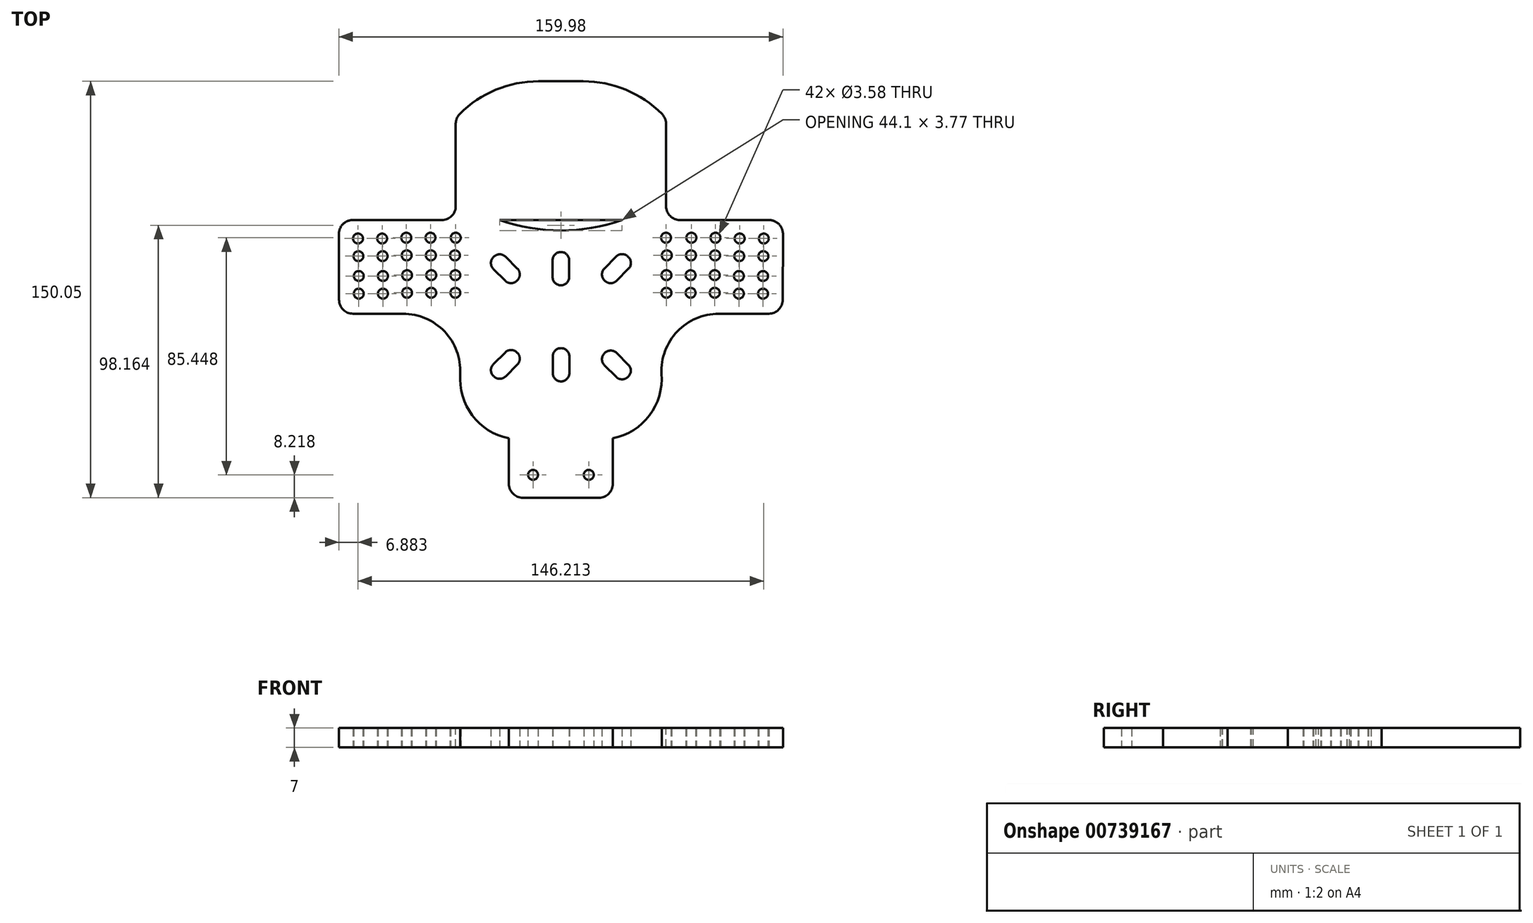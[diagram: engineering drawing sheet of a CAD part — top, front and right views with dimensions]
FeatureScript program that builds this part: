
annotation { "Feature Type Name" : "Feature", "Feature Type Description" : "" }
export const myFeature = defineFeature(function(context is Context, id is Id, definition is map)
    precondition{}
    {
        {
            var Q0;
            Q0=qCreatedBy(makeId("Top.planeOp"),FACE);
            var sketch = newSketch(context, id + "F0", { "sketchPlane" : qUnion([Q0])});
            skLineSegment(sketch, "E0", {"start": v(-79.91, 0) * mm, "end": v(79.75, 0) * mm, "construction": true});
            skLineSegment(sketch, "E1", {"start": v(-22.05, 33.69) * mm, "end": v(-80, 33.69) * mm});
            skLineSegment(sketch, "E2", {"start": v(-80, 33.69) * mm, "end": v(-79.91, -0.06) * mm});
            skLineSegment(sketch, "E3", {"start": v(-79.91, -0.06) * mm, "end": v(-56.88, -0.06) * mm});
            skArc(sketch, "E4", {"start": v(-36.27, -21.72) * mm, "mid": v(-41.93, -6.47) * mm, "end": v(-56.88, -0.06) * mm});
            skArc(sketch, "E5", {"start": v(-36.27, -21.72) * mm, "mid": v(-31.92, -36.69) * mm, "end": v(-18.73, -45) * mm});
            skLineSegment(sketch, "E6", {"start": v(-18.73, -45) * mm, "end": v(-18.73, -66.36) * mm});
            skLineSegment(sketch, "E7", {"start": v(-18.73, -66.36) * mm, "end": v(0, -66.36) * mm});
            skCircle(sketch, "E8", {"center": v(-73.1, 27.02) * mm, "radius": 1.8 * mm});
            skCircle(sketch, "E9", {"center": v(-72.82, 13.52) * mm, "radius": 1.8 * mm});
            skCircle(sketch, "E10", {"center": v(-72.95, 20.67) * mm, "radius": 1.8 * mm});
            skCircle(sketch, "E11", {"center": v(-72.82, 7.17) * mm, "radius": 1.8 * mm});
            skCircle(sketch, "E12", {"center": v(-64.4, 27.02) * mm, "radius": 1.8 * mm});
            skCircle(sketch, "E13", {"center": v(-64.12, 13.52) * mm, "radius": 1.8 * mm});
            skCircle(sketch, "E14", {"center": v(-64.25, 20.67) * mm, "radius": 1.8 * mm});
            skCircle(sketch, "E15", {"center": v(-64.12, 7.17) * mm, "radius": 1.8 * mm});
            skCircle(sketch, "E16", {"center": v(-55.7, 27.3) * mm, "radius": 1.8 * mm});
            skCircle(sketch, "E17", {"center": v(-55.42, 13.8) * mm, "radius": 1.8 * mm});
            skCircle(sketch, "E18", {"center": v(-55.55, 20.95) * mm, "radius": 1.8 * mm});
            skCircle(sketch, "E19", {"center": v(-55.42, 7.45) * mm, "radius": 1.8 * mm});
            skCircle(sketch, "E20", {"center": v(-47, 27.3) * mm, "radius": 1.8 * mm});
            skCircle(sketch, "E21", {"center": v(-46.72, 13.8) * mm, "radius": 1.8 * mm});
            skCircle(sketch, "E22", {"center": v(-46.85, 20.95) * mm, "radius": 1.8 * mm});
            skCircle(sketch, "E23", {"center": v(-46.72, 7.45) * mm, "radius": 1.8 * mm});
            skCircle(sketch, "E24", {"center": v(-37.88, 27.3) * mm, "radius": 1.8 * mm});
            skCircle(sketch, "E25", {"center": v(-38.02, 13.8) * mm, "radius": 1.8 * mm});
            skCircle(sketch, "E26", {"center": v(-38.15, 20.95) * mm, "radius": 1.8 * mm});
            skCircle(sketch, "E27", {"center": v(-38.02, 7.45) * mm, "radius": 1.8 * mm});
            skCircle(sketch, "E28.MirrorC", {"center": v(37.88, 27.3) * mm, "radius": 1.8 * mm});
            skCircle(sketch, "E29.MirrorC", {"center": v(38.02, 13.8) * mm, "radius": 1.8 * mm});
            skCircle(sketch, "E30.MirrorC", {"center": v(55.55, 20.95) * mm, "radius": 1.8 * mm});
            skCircle(sketch, "E31.MirrorC", {"center": v(55.42, 13.8) * mm, "radius": 1.8 * mm});
            skCircle(sketch, "E32.MirrorC", {"center": v(38.15, 20.95) * mm, "radius": 1.8 * mm});
            skCircle(sketch, "E33.MirrorC", {"center": v(55.42, 7.45) * mm, "radius": 1.8 * mm});
            skCircle(sketch, "E34.MirrorC", {"center": v(38.02, 7.45) * mm, "radius": 1.8 * mm});
            skCircle(sketch, "E35.MirrorC", {"center": v(47, 27.3) * mm, "radius": 1.8 * mm});
            skCircle(sketch, "E36.MirrorC", {"center": v(46.72, 13.8) * mm, "radius": 1.8 * mm});
            skCircle(sketch, "E37.MirrorC", {"center": v(64.4, 27.02) * mm, "radius": 1.8 * mm});
            skCircle(sketch, "E38.MirrorC", {"center": v(64.12, 13.52) * mm, "radius": 1.8 * mm});
            skCircle(sketch, "E39.MirrorC", {"center": v(64.25, 20.67) * mm, "radius": 1.8 * mm});
            skCircle(sketch, "E40.MirrorC", {"center": v(55.7, 27.3) * mm, "radius": 1.8 * mm});
            skCircle(sketch, "E41.MirrorC", {"center": v(46.72, 7.45) * mm, "radius": 1.8 * mm});
            skCircle(sketch, "E42.MirrorC", {"center": v(73.1, 27.02) * mm, "radius": 1.8 * mm});
            skCircle(sketch, "E43.MirrorC", {"center": v(46.85, 20.95) * mm, "radius": 1.8 * mm});
            skCircle(sketch, "E44.MirrorC", {"center": v(72.82, 13.52) * mm, "radius": 1.8 * mm});
            skCircle(sketch, "E45.MirrorC", {"center": v(64.12, 7.17) * mm, "radius": 1.8 * mm});
            skCircle(sketch, "E46.MirrorC", {"center": v(72.95, 20.67) * mm, "radius": 1.8 * mm});
            skCircle(sketch, "E47.MirrorC", {"center": v(72.82, 7.17) * mm, "radius": 1.8 * mm});
            skLineSegment(sketch, "E48.MirrorCS", {"start": v(18.73, -45) * mm, "end": v(18.73, -66.36) * mm});
            skLineSegment(sketch, "E49.MirrorCS", {"start": v(18.73, -66.36) * mm, "end": v(0, -66.36) * mm});
            skArc(sketch, "E50.MirrorCS", {"start": v(36.27, -21.72) * mm, "mid": v(41.93, -6.47) * mm, "end": v(56.88, -0.06) * mm});
            skLineSegment(sketch, "E51.MirrorCS", {"start": v(79.91, -0.06) * mm, "end": v(56.88, -0.06) * mm});
            skLineSegment(sketch, "E52.MirrorCS", {"start": v(80, 33.69) * mm, "end": v(79.91, -0.06) * mm});
            skLineSegment(sketch, "E53.MirrorCS", {"start": v(0, 33.69) * mm, "end": v(0.15, 33.69) * mm});
            skArc(sketch, "E54.MirrorCS", {"start": v(36.27, -21.72) * mm, "mid": v(31.92, -36.69) * mm, "end": v(18.73, -45) * mm});
            skLineSegment(sketch, "E55.MirrorCS", {"start": v(26.43, 18.19) * mm, "end": v(22.05, 22.7) * mm});
            skLineSegment(sketch, "E56.MirrorCS", {"start": v(-17.95, 9.7) * mm, "end": v(-13.57, 14.08) * mm});
            skLineSegment(sketch, "E57.MirrorCS", {"start": v(-26.43, 18.19) * mm, "end": v(-22.05, 22.57) * mm});
            skLineSegment(sketch, "E58.MirrorCS", {"start": v(17.95, 9.7) * mm, "end": v(13.57, 14.08) * mm});
            skLineSegment(sketch, "E59.MirrorCS", {"start": v(22.05, 22.7) * mm, "end": v(13.57, 14.08) * mm});
            skLineSegment(sketch, "E60.MirrorCS", {"start": v(-22.05, 22.57) * mm, "end": v(-13.57, 14.08) * mm});
            skLineSegment(sketch, "E61.MirrorCS", {"start": v(26.43, 18.19) * mm, "end": v(17.95, 9.7) * mm});
            skLineSegment(sketch, "E62.MirrorCS", {"start": v(-26.43, 18.19) * mm, "end": v(-17.95, 9.7) * mm});
            skLineSegment(sketch, "E63.bottom", {"start": v(-3, 22.17) * mm, "end": v(3, 22.17) * mm});
            skLineSegment(sketch, "E63.top", {"start": v(-3, 10.17) * mm, "end": v(3, 10.17) * mm});
            skLineSegment(sketch, "E63.left", {"start": v(-3, 22.17) * mm, "end": v(-3, 10.17) * mm});
            skLineSegment(sketch, "E63.right", {"start": v(3, 22.17) * mm, "end": v(3, 10.17) * mm});
            skCircle(sketch, "E64", {"center": v(-10.05, -58.14) * mm, "radius": 1.8 * mm});
            skArc(sketch, "E65", {"start": v(-22.05, 33.69) * mm, "mid": v(0, 29.92) * mm, "end": v(22.05, 33.69) * mm});
            skLineSegment(sketch, "E66.trimOffspring", {"start": v(22.05, 33.69) * mm, "end": v(80, 33.69) * mm});
            skLineSegment(sketch, "E67", {"start": v(17.95, 9.7) * mm, "end": v(22.05, 22.7) * mm, "construction": true});
            skLineSegment(sketch, "E68", {"start": v(13.57, 14.08) * mm, "end": v(26.43, 18.19) * mm, "construction": true});
            skLineSegment(sketch, "E69", {"start": v(-3, 10.17) * mm, "end": v(3, 22.17) * mm, "construction": true});
            skLineSegment(sketch, "E70", {"start": v(-3, 22.17) * mm, "end": v(3, 10.17) * mm, "construction": true});
            skPoint(sketch, "E71", {"position": v(-20, 16.13) * mm});
            skPoint(sketch, "E72", {"position": v(0, 16.17) * mm});
            skPoint(sketch, "E73", {"position": v(20, 16.2) * mm});
            skLineSegment(sketch, "E74.MirrorCS", {"start": v(-2.94, -24.47) * mm, "end": v(3.06, -12.47) * mm, "construction": true});
            skLineSegment(sketch, "E75.MirrorCS", {"start": v(-26.43, -20.39) * mm, "end": v(-17.95, -11.9) * mm});
            skLineSegment(sketch, "E76.MirrorCS", {"start": v(13.57, -16.48) * mm, "end": v(26.43, -20.58) * mm, "construction": true});
            skLineSegment(sketch, "E77.MirrorCS", {"start": v(-17.95, -11.9) * mm, "end": v(-13.57, -16.28) * mm});
            skLineSegment(sketch, "E78.MirrorCS", {"start": v(-2.94, -12.47) * mm, "end": v(3.06, -24.47) * mm, "construction": true});
            skLineSegment(sketch, "E79.MirrorCS", {"start": v(-2.94, -24.47) * mm, "end": v(-2.94, -12.47) * mm});
            skLineSegment(sketch, "E80.MirrorCS", {"start": v(-2.94, -12.47) * mm, "end": v(3.06, -12.47) * mm});
            skLineSegment(sketch, "E81.MirrorCS", {"start": v(26.43, -20.58) * mm, "end": v(17.95, -12.1) * mm});
            skLineSegment(sketch, "E82.MirrorCS", {"start": v(-22.05, -24.77) * mm, "end": v(-13.57, -16.28) * mm});
            skLineSegment(sketch, "E83.MirrorCS", {"start": v(17.95, -12.1) * mm, "end": v(22.05, -24.97) * mm, "construction": true});
            skLineSegment(sketch, "E84.MirrorCS", {"start": v(-26.43, -20.39) * mm, "end": v(-22.05, -24.77) * mm});
            skLineSegment(sketch, "E85.MirrorCS", {"start": v(3.06, -24.47) * mm, "end": v(3.06, -12.47) * mm});
            skPoint(sketch, "E86.MirrorP", {"position": v(20.06, -18.44) * mm});
            skPoint(sketch, "E87.MirrorP", {"position": v(-19.94, -18.5) * mm});
            skPoint(sketch, "E88.MirrorP", {"position": v(0.06, -18.47) * mm});
            skLineSegment(sketch, "E89.MirrorCS", {"start": v(22.05, -24.97) * mm, "end": v(13.57, -16.48) * mm});
            skLineSegment(sketch, "E90.MirrorCS", {"start": v(26.43, -20.58) * mm, "end": v(22.05, -24.97) * mm});
            skLineSegment(sketch, "E91.MirrorCS", {"start": v(17.95, -12.1) * mm, "end": v(13.57, -16.48) * mm});
            skLineSegment(sketch, "E92.MirrorCS", {"start": v(-2.94, -24.47) * mm, "end": v(3.06, -24.47) * mm});
            skCircle(sketch, "E93.MirrorC", {"center": v(10.05, -58.14) * mm, "radius": 1.8 * mm});
            skLineSegment(sketch, "E94.bottom", {"start": v(-37.88, 33.69) * mm, "end": v(37.88, 33.69) * mm});
            skLineSegment(sketch, "E94.top", {"start": v(-28.16, 83.69) * mm, "end": v(28.16, 83.69) * mm});
            skLineSegment(sketch, "E94.left", {"start": v(-37.88, 33.69) * mm, "end": v(-37.88, 70.36) * mm});
            skLineSegment(sketch, "E94.right", {"start": v(37.88, 33.69) * mm, "end": v(37.88, 70.36) * mm});
            skLineSegment(sketch, "E95", {"start": v(-37.88, 70.36) * mm, "end": v(-28.16, 83.69) * mm});
            skLineSegment(sketch, "E96.MirrorCS", {"start": v(28.16, 83.69) * mm, "end": v(-28.16, 83.69) * mm});
            skLineSegment(sketch, "E97.MirrorCS", {"start": v(37.88, 70.36) * mm, "end": v(28.16, 83.69) * mm});
            skSolve(sketch);
        }
        {
            var Q0;
            {var subQ1=sQuery(id+"F0.wireOp",EDGE,"E53.MirrorCS");var subQ13=sQuery(id+"F0.wireOp",EDGE,"E2");Q0=qUnion([makeQuery(id+"F0.imprint","IMPRINT",FACE,{"disambiguationData":[TD([[makeQuery(id+"F0.imprint","IMPRINT",EDGE,{"derivedFrom":subQ13}),1.0]])]}),makeQuery(id+"F0.imprint","IMPRINT",FACE,{"disambiguationData":[TD([[makeQuery(id+"F0.imprint","IMPRINT",EDGE,{"derivedFrom":subQ1}),1.0]])]})]);}
            extrude(context, id + "F1", {"entities" : qUnion([Q0]), "depth" : 7 * mm, "offsetDistance" : 25 * mm});
        }
        {
            var Q0;
            Q0=makeQuery(id+"F1.opExtrude","SWEPT_EDGE",EDGE,{"disambiguationData":[OSD([sQuery(id+"F0.wireOp",EDGE,"E1"),sQuery(id+"F0.wireOp",EDGE,"E2")])]});
            var Q1;
            Q1=makeQuery(id+"F1.opExtrude","SWEPT_EDGE",EDGE,{"disambiguationData":[OSD([sQuery(id+"F0.wireOp",EDGE,"E2"),sQuery(id+"F0.wireOp",EDGE,"E3")])]});
            var Q2;
            Q2=makeQuery(id+"F1.opExtrude","SWEPT_EDGE",EDGE,{"disambiguationData":[OSD([sQuery(id+"F0.wireOp",EDGE,"E6"),sQuery(id+"F0.wireOp",EDGE,"E7")])]});
            var Q3;
            Q3=makeQuery(id+"F1.opExtrude","SWEPT_EDGE",EDGE,{"disambiguationData":[OSD([sQuery(id+"F0.wireOp",EDGE,"E48.MirrorCS"),sQuery(id+"F0.wireOp",EDGE,"E49.MirrorCS")])]});
            var Q4;
            Q4=makeQuery(id+"F1.opExtrude","SWEPT_EDGE",EDGE,{"disambiguationData":[OSD([sQuery(id+"F0.wireOp",EDGE,"E51.MirrorCS"),sQuery(id+"F0.wireOp",EDGE,"E52.MirrorCS")])]});
            var Q5;
            Q5=makeQuery(id+"F1.opExtrude","SWEPT_EDGE",EDGE,{"disambiguationData":[OSD([sQuery(id+"F0.wireOp",EDGE,"E52.MirrorCS"),sQuery(id+"F0.wireOp",EDGE,"E66.trimOffspring")])]});
            fillet(context, id + "F2", {"entities" : qUnion([Q0, Q1, Q2, Q3, Q4, Q5]), "radius" : 5 * mm, "tangentPropagation" : true, "allowEdgeOverflow" : false});
        }
        {
            var Q0;
            Q0=makeQuery(id+"F1.opExtrude","SWEPT_EDGE",EDGE,{"disambiguationData":[OSD([sQuery(id+"F0.wireOp",EDGE,"E57.MirrorCS"),sQuery(id+"F0.wireOp",EDGE,"E60.MirrorCS")])]});
            var Q1;
            Q1=makeQuery(id+"F1.opExtrude","SWEPT_EDGE",EDGE,{"disambiguationData":[OSD([sQuery(id+"F0.wireOp",EDGE,"E56.MirrorCS"),sQuery(id+"F0.wireOp",EDGE,"E60.MirrorCS")])]});
            var Q2;
            Q2=makeQuery(id+"F1.opExtrude","SWEPT_EDGE",EDGE,{"disambiguationData":[OSD([sQuery(id+"F0.wireOp",EDGE,"E55.MirrorCS"),sQuery(id+"F0.wireOp",EDGE,"E61.MirrorCS")])]});
            var Q3;
            Q3=makeQuery(id+"F1.opExtrude","SWEPT_EDGE",EDGE,{"disambiguationData":[OSD([sQuery(id+"F0.wireOp",EDGE,"E55.MirrorCS"),sQuery(id+"F0.wireOp",EDGE,"E59.MirrorCS")])]});
            var Q4;
            Q4=makeQuery(id+"F1.opExtrude","SWEPT_EDGE",EDGE,{"disambiguationData":[OSD([sQuery(id+"F0.wireOp",EDGE,"E63.bottom"),sQuery(id+"F0.wireOp",EDGE,"E63.right")])]});
            var Q5;
            Q5=makeQuery(id+"F1.opExtrude","SWEPT_EDGE",EDGE,{"disambiguationData":[OSD([sQuery(id+"F0.wireOp",EDGE,"E63.bottom"),sQuery(id+"F0.wireOp",EDGE,"E63.left")])]});
            var Q6;
            Q6=makeQuery(id+"F1.opExtrude","SWEPT_EDGE",EDGE,{"disambiguationData":[OSD([sQuery(id+"F0.wireOp",EDGE,"E57.MirrorCS"),sQuery(id+"F0.wireOp",EDGE,"E62.MirrorCS")])]});
            var Q7;
            Q7=makeQuery(id+"F1.opExtrude","SWEPT_EDGE",EDGE,{"disambiguationData":[OSD([sQuery(id+"F0.wireOp",EDGE,"E63.top"),sQuery(id+"F0.wireOp",EDGE,"E63.left")])]});
            var Q8;
            Q8=makeQuery(id+"F1.opExtrude","SWEPT_EDGE",EDGE,{"disambiguationData":[OSD([sQuery(id+"F0.wireOp",EDGE,"E56.MirrorCS"),sQuery(id+"F0.wireOp",EDGE,"E62.MirrorCS")])]});
            var Q9;
            Q9=makeQuery(id+"F1.opExtrude","SWEPT_EDGE",EDGE,{"disambiguationData":[OSD([sQuery(id+"F0.wireOp",EDGE,"E58.MirrorCS"),sQuery(id+"F0.wireOp",EDGE,"E61.MirrorCS")])]});
            var Q10;
            Q10=makeQuery(id+"F1.opExtrude","SWEPT_EDGE",EDGE,{"disambiguationData":[OSD([sQuery(id+"F0.wireOp",EDGE,"E58.MirrorCS"),sQuery(id+"F0.wireOp",EDGE,"E59.MirrorCS")])]});
            var Q11;
            Q11=makeQuery(id+"F1.opExtrude","SWEPT_EDGE",EDGE,{"disambiguationData":[OSD([sQuery(id+"F0.wireOp",EDGE,"E63.top"),sQuery(id+"F0.wireOp",EDGE,"E63.right")])]});
            var Q12;
            Q12=makeQuery(id+"F1.opExtrude","SWEPT_EDGE",EDGE,{"disambiguationData":[OSD([sQuery(id+"F0.wireOp",EDGE,"E89.MirrorCS"),sQuery(id+"F0.wireOp",EDGE,"E91.MirrorCS")])]});
            var Q13;
            Q13=makeQuery(id+"F1.opExtrude","SWEPT_EDGE",EDGE,{"disambiguationData":[OSD([sQuery(id+"F0.wireOp",EDGE,"E79.MirrorCS"),sQuery(id+"F0.wireOp",EDGE,"E92.MirrorCS")])]});
            var Q14;
            Q14=makeQuery(id+"F1.opExtrude","SWEPT_EDGE",EDGE,{"disambiguationData":[OSD([sQuery(id+"F0.wireOp",EDGE,"E79.MirrorCS"),sQuery(id+"F0.wireOp",EDGE,"E80.MirrorCS")])]});
            var Q15;
            Q15=makeQuery(id+"F1.opExtrude","SWEPT_EDGE",EDGE,{"disambiguationData":[OSD([sQuery(id+"F0.wireOp",EDGE,"E81.MirrorCS"),sQuery(id+"F0.wireOp",EDGE,"E91.MirrorCS")])]});
            var Q16;
            Q16=makeQuery(id+"F1.opExtrude","SWEPT_EDGE",EDGE,{"disambiguationData":[OSD([sQuery(id+"F0.wireOp",EDGE,"E80.MirrorCS"),sQuery(id+"F0.wireOp",EDGE,"E85.MirrorCS")])]});
            var Q17;
            Q17=makeQuery(id+"F1.opExtrude","SWEPT_EDGE",EDGE,{"disambiguationData":[OSD([sQuery(id+"F0.wireOp",EDGE,"E81.MirrorCS"),sQuery(id+"F0.wireOp",EDGE,"E90.MirrorCS")])]});
            var Q18;
            Q18=makeQuery(id+"F1.opExtrude","SWEPT_EDGE",EDGE,{"disambiguationData":[OSD([sQuery(id+"F0.wireOp",EDGE,"E89.MirrorCS"),sQuery(id+"F0.wireOp",EDGE,"E90.MirrorCS")])]});
            var Q19;
            Q19=makeQuery(id+"F1.opExtrude","SWEPT_EDGE",EDGE,{"disambiguationData":[OSD([sQuery(id+"F0.wireOp",EDGE,"E85.MirrorCS"),sQuery(id+"F0.wireOp",EDGE,"E92.MirrorCS")])]});
            var Q20;
            Q20=makeQuery(id+"F1.opExtrude","SWEPT_EDGE",EDGE,{"disambiguationData":[OSD([sQuery(id+"F0.wireOp",EDGE,"E75.MirrorCS"),sQuery(id+"F0.wireOp",EDGE,"E77.MirrorCS")])]});
            var Q21;
            Q21=makeQuery(id+"F1.opExtrude","SWEPT_EDGE",EDGE,{"disambiguationData":[OSD([sQuery(id+"F0.wireOp",EDGE,"E75.MirrorCS"),sQuery(id+"F0.wireOp",EDGE,"E84.MirrorCS")])]});
            var Q22;
            Q22=makeQuery(id+"F1.opExtrude","SWEPT_EDGE",EDGE,{"disambiguationData":[OSD([sQuery(id+"F0.wireOp",EDGE,"E77.MirrorCS"),sQuery(id+"F0.wireOp",EDGE,"E82.MirrorCS")])]});
            var Q23;
            Q23=makeQuery(id+"F1.opExtrude","SWEPT_EDGE",EDGE,{"disambiguationData":[OSD([sQuery(id+"F0.wireOp",EDGE,"E82.MirrorCS"),sQuery(id+"F0.wireOp",EDGE,"E84.MirrorCS")])]});
            fillet(context, id + "F3", {"entities" : qUnion([Q0, Q1, Q2, Q3, Q4, Q5, Q6, Q7, Q8, Q9, Q10, Q11, Q12, Q13, Q14, Q15, Q16, Q17, Q18, Q19, Q20, Q21, Q22, Q23]), "radius" : 3 * mm, "tangentPropagation" : true, "allowEdgeOverflow" : false});
        }
        {
            var Q0;
            Q0=makeQuery(id+"F1.opExtrude","SWEPT_EDGE",EDGE,{"disambiguationData":[OSD([sQuery(id+"F0.wireOp",EDGE,"E1"),sQuery(id+"F0.wireOp",EDGE,"E94.left")])]});
            fillet(context, id + "F4", {"entities" : qUnion([Q0]), "radius" : 5 * mm, "tangentPropagation" : true, "allowEdgeOverflow" : false});
        }
        {
            var Q0;
            Q0=makeQuery(id+"F1.opExtrude","SWEPT_EDGE",EDGE,{"disambiguationData":[OSD([sQuery(id+"F0.wireOp",EDGE,"E66.trimOffspring"),sQuery(id+"F0.wireOp",EDGE,"E94.right")])]});
            fillet(context, id + "F5", {"entities" : qUnion([Q0]), "radius" : 5 * mm, "tangentPropagation" : true, "allowEdgeOverflow" : false});
        }
        {
            var Q0;
            Q0=makeQuery(id+"F1.opExtrude","SWEPT_EDGE",EDGE,{"disambiguationData":[OSD([sQuery(id+"F0.wireOp",EDGE,"E94.top"),sQuery(id+"F0.wireOp",EDGE,"E95")])]});
            var Q1;
            Q1=makeQuery(id+"Fi5Zi2aroou93jv_1.opFillet","BLEND_FACE",FACE,{"disambiguationData":[OSD([sQuery(id+"F0.wireOp",EDGE,"E94.left"),sQuery(id+"F0.wireOp",EDGE,"E95")])]});
            var Q2;
            Q2=makeQuery(id+"F1.opExtrude","SWEPT_EDGE",EDGE,{"disambiguationData":[OSD([sQuery(id+"F0.wireOp",EDGE,"E94.top"),sQuery(id+"F0.wireOp",EDGE,"E97.MirrorCS")])]});
            fillet(context, id + "F6", {"entities" : qUnion([Q0, Q1, Q2]), "radius" : 40 * mm, "tangentPropagation" : true, "allowEdgeOverflow" : false});
        }
        {
            var Q0;
            Q0=makeQuery(id+"F6.opFillet","BLEND_EDGE",EDGE,{"blendedFrom":[makeQuery(id+"F1.opExtrude","SWEPT_EDGE",EDGE,{"disambiguationData":[OSD([sQuery(id+"F0.wireOp",EDGE,"E94.top"),sQuery(id+"F0.wireOp",EDGE,"E95")])]}),makeQuery(id+"F1.opExtrude","SWEPT_FACE",FACE,{"disambiguationData":[OSD([sQuery(id+"F0.wireOp",EDGE,"E94.left")])]})],"blendedInto":[makeQuery(id+"F1.opExtrude","SWEPT_FACE",FACE,{"disambiguationData":[OSD([sQuery(id+"F0.wireOp",EDGE,"E94.left")])]})]});
            fillet(context, id + "F7", {"entities" : qUnion([Q0]), "radius" : 5 * mm, "tangentPropagation" : true, "allowEdgeOverflow" : false});
        }
        {
            var Q0;
            Q0=makeQuery(id+"F6.opFillet","BLEND_EDGE",EDGE,{"blendedFrom":[makeQuery(id+"F1.opExtrude","SWEPT_EDGE",EDGE,{"disambiguationData":[OSD([sQuery(id+"F0.wireOp",EDGE,"E94.top"),sQuery(id+"F0.wireOp",EDGE,"E97.MirrorCS")])]}),makeQuery(id+"F1.opExtrude","SWEPT_FACE",FACE,{"disambiguationData":[OSD([sQuery(id+"F0.wireOp",EDGE,"E94.right")])]})],"blendedInto":[makeQuery(id+"F1.opExtrude","SWEPT_FACE",FACE,{"disambiguationData":[OSD([sQuery(id+"F0.wireOp",EDGE,"E94.right")])]})]});
            fillet(context, id + "F8", {"entities" : qUnion([Q0]), "radius" : 5 * mm, "tangentPropagation" : true, "allowEdgeOverflow" : false});
        }
    });
